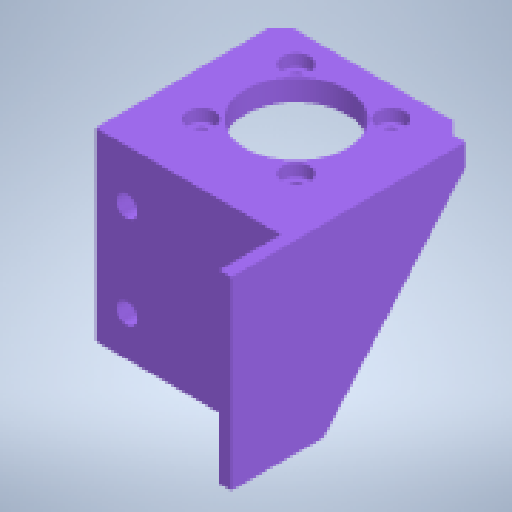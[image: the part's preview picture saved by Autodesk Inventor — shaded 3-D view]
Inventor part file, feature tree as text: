
AUTODESK INVENTOR PART (.ipt)
format: ipt  version: 2025.1 (Build 291241000, 241)  size: 301,056 bytes
history: native  units: mm
features: sketch x5, extrude x3, hole x2
ambient origin geometry x8: Origin, YZ Plane, XZ Plane, XY Plane, X Axis, Y Axis, Z Axis, Center Point
bodies: Solide1 (feature_tree)
feature tree (10):
  extrude  "Extrusion1"  Depth=25.0mm
  hole  "Perçage1"  [1 undecoded]
  extrude  "Extrusion2"  Depth=16.5mm
  hole  "Perçage2"  [1 undecoded]
  extrude  "Extrusion4"  Depth=2.0mm
  sketch  "Esquisse1"
  sketch  "Esquisse2"
  sketch  "Esquisse3"
  sketch  "Esquisse5"
  sketch  "Esquisse6"
note: 2 required parameter values undecoded (feature->parameter linkage not recoverable at this tier; creation-order binding heuristic only, values carry confidence <= 0.55)
